# Revit family: M_Pojedyncze - panelowe 1
name_source: partatom
category: Doors
revit_build: Autodesk Revit 2014 (Build: 20130126_1515(x64)
units: mm (PartAtom-declared; Revit-internal decimal feet)

## types (7) — shared parameters
Analytic Construction = Metal
Construction Type Id = MDRZWI
Function = Interior
Heat Transfer Coefficient (U) = 3.7021 W/(m²·K)
Materiał drzwi = Drzwi - panel
Materiał ramy = Drzwi - rama
Panel górny = 915 mm  [stored 3.00197 ft]
Rzut przycięcia - wewnętrzny = 25 mm  [stored 0.082021 ft]
Rzut przycięcia - zewnętrzny = 25 mm  [stored 0.082021 ft]
Szerokość poręczy - góra = 150 mm
Szerokość poręczy - podstawa = 175 mm  [stored 0.574147 ft]
Szerokość poręczy - środek = 100 mm  [stored 0.328084 ft]
Szerokość przycięcia = 76 mm  [stored 0.249344 ft]
Szerokość ramiaka = 127 mm  [stored 0.416667 ft]
Thickness = 51 mm  [stored 0.167323 ft]
Wall Closure = By host
zero-valued in all types: Solar Heat Gain Coefficient, Visual Light Transmittance

## per-type parameters (varying)
| type | Height | Width |
| 0915 x 2134 mm | 2134 mm  [stored 7.00131 ft] | 915 mm  [stored 3.00197 ft] |
| 0864 x 2134 mm | 2134 mm  [stored 7.00131 ft] | 864 mm |
| 0813 x 2134 mm | 2134 mm  [stored 7.00131 ft] | 813 mm  [stored 2.66732 ft] |
| 0762 x 2134 mm | 2134 mm  [stored 7.00131 ft] | 762 mm |
| 0762 x 2032 mm | 2032 mm  [stored 6.66667 ft] | 762 mm |
| 0915 x 2032 mm | 2032 mm  [stored 6.66667 ft] | 915 mm  [stored 3.00197 ft] |
| 0864 x 2032 mm | 2032 mm  [stored 6.66667 ft] | 864 mm |

note: [stored X ft] marks values corroborated as IEEE doubles in the binary element streams (Revit-internal decimal feet)
